# Revit family: LWplc_Latchwaysplc_FallArrestSystemGuidedAnchorLine_GreenRoofType
name_source: partatom
category: Generic Models
revit_build: Autodesk Revit 2014 (Build: 20130308_1515(x64)
units: mm (PartAtom-declared; Revit-internal decimal feet)

## types (4) — shared parameters
AssetType = Fixed
AttachmentDeviceGuide = www.latchways.com/BIM/Latchways_Attachment_Device_Guide.pdf
CFPMaterial = Aluminum
Default Elevation = 1219 mm
Description = Latchways ManSafe® for Green Roofing, using Constant Force posts
DurationUnit = year
FireExit = No
Height = 248 mm  [stored 0.813648 ft]
IfcExportAs = NOTDEFINED
IfcExportType = IfcTransportElement
Length = 532 mm
ManSafeForRoofingBrochure = www.latchways.com/BIM/MansafeForRoofing.pdf
ManufacturerName = Latchways plc
ManufacturerURL = www.latchways.com
Material = Dome: 316s Stainless Steel; Baseplate: Aluminium, PVC coated
NBSDescription = Fall arrest system - guided anchor line
NBSReference = 80-50-25/110
NominalLength = 532 mm
NominalWidth = 375 mm
PreInstallationSurvey = Required
ProductSpecification = www.latchways.com/BIM/Latchways_CFP_GreenRoofs_NBS_Specifications.doc
SystemMaintenance = Annual service to be completed by Latchways registered installers in accordance with BS7883:2005
SystemManufacturer = Latchways plc
URL = www.latchways.com
Uniclass2 = 80-30-25/135
Version = 1
WarrantyDurationUnit = year
Width = 375 mm

## per-type parameters (varying)
| type | BIMObjectName | CFPColour | Color | FixingDetail | Model | ModelNumber | ModelReference | Name | NominalHeight | ProductInformation | Size | cap_value | weather_cap_on/off |
| CFP Green Roof (PVC) | LWplc_Latchwaysplc_FallArrestSystemGuidedAnchorLine_GreenRoofType_PVC | LWplc_Latchwaysplc_PVCCoated_RAL7046 | Dome: Stainless Steel, Electro Polished; Baseplate: RAL7046 | www.latchways.com/BIM/Latchways_CFP_GreenRoofs_FixingDetail.pdf | 65691-00 | 65691-00 | Constant Force Post - Green Roof (PVC) | FallArrestSystemGuidedAnchorLine_GreenRoofType_PVC_Latchwaysplc | 259 mm  [stored 0.849738 ft] | www.latchways.com/BIM/65691-00_LatchwaysConstantForcePost_GreenRoof_PVC-Membrane.pdf | 532 x 375 x 259mm | 0 | No |
| CFP Bituminous Green Roofing | LWplc_Latchwaysplc_FallArrestSystemGuidedAnchorLine_GreenRoofType_Bituminous | LWplc_Latchwaysplc_PVCCoated_RAL7038 | Dome: Stainless Steel, Electro Polished; Baseplate: RAL7038 | www.latchways.com/BIM/Latchways_CFP_GreenRoofs_FixingDetail.pdf | 65692-00 | 65692-00 | Constant Force Post - Bituminous Green Roofing | FallArrestSystemGuidedAnchorLine_GreenRoofType_Bituminous_Latchwaysplc | 259 mm  [stored 0.849738 ft] | www.latchways.com/BIM/65692-00_LatchwaysConstantForcePost_GreenRoof_Bituminous.pdf | 532 x 375 x 259mm | 0 | No |
| CFP TPO (Talisman) Green Roofing | LWplc_Latchwaysplc_FallArrestSystemGuidedAnchorLine_GreenRoofType_TPO | LWplc_Latchwaysplc_PVCCoated_RAL7038 | Dome: Stainless Steel, Electro Polished; Baseplate: RAL7038 | www.latchways.com/BIM/Latchways_CFP_GreenRoofs_FixingDetail.pdf | 65693-00 | 65693-00 | Constant Force Post - TPO (Talisman) Green Roofing | FallArrestSystemGuidedAnchorLine_GreenRoofType_TPO_Latchwaysplc | 259 mm  [stored 0.849738 ft] | www.latchways.com/BIM/65693-00_LatchwaysConstantForcePost_GreenRoof_TPO_Talisman_Membrane.pdf | 532 x 375 x 259mm | 0 | No |
| CFP Weathering Cap Green Roofing | LWplc_Latchwaysplc_FallArrestSystemGuidedAnchorLine_GreenRoofType_WeatherCap | LWplc_Latchwaysplc_PVCCoated_RAL9005 | Dome: Stainless Steel, Electro Polished; Baseplate & Cap: RAL9005 | www.latchways.com/BIM/LaLatchways_CFP_GreenRoofs_FixingDetail.pdf | 65694-00 | 65694-00 | Constant Force Post - Weathering Cap Green Roofing | FallArrestSystemGuidedAnchorLine_GreenRoofType_WeatherCap_Latchwaysplc | 262 mm  [stored 0.85958 ft] | www.latchways.com/BIM/65694-00_LatchwaysConstantForcePost_GreenRoof_WeatheringCap-NonPVC.pdf | 532 x 375 x 262mm | 1 | Yes |

note: [stored X ft] marks values corroborated as IEEE doubles in the binary element streams (Revit-internal decimal feet)

## geometry (parser evidence)
native form markers: Extrusion x1, Sweep x6
no freeform markers — native parametric forms only
